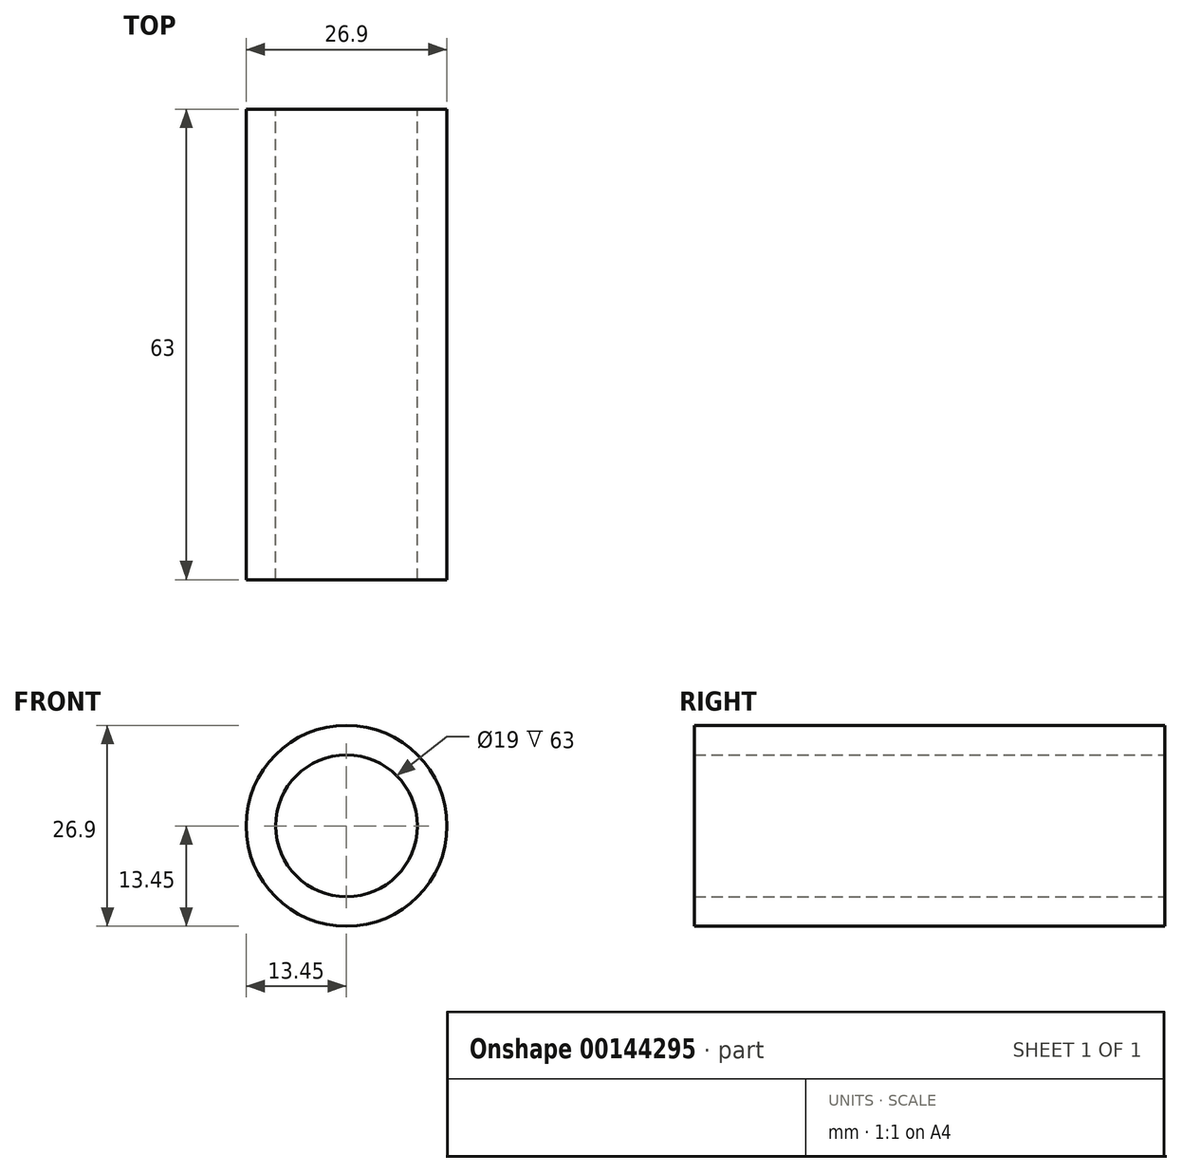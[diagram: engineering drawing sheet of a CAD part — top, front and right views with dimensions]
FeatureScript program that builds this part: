
annotation { "Feature Type Name" : "Feature", "Feature Type Description" : "" }
export const myFeature = defineFeature(function(context is Context, id is Id, definition is map)
    precondition{}
    {
        {
            var Q0;
            Q0=qCreatedBy(makeId("Front.planeOp"),FACE);
            var sketch = newSketch(context, id + "F0", { "sketchPlane" : qUnion([Q0])});
            skCircle(sketch, "E0", {"center": v(0, 0) * mm, "radius": 13.45 * mm});
            skCircle(sketch, "E1", {"center": v(0, 0) * mm, "radius": 9.5 * mm});
            skSolve(sketch);
        }
        {
            var Q0;
            Q0=makeQuery(id+"F0.imprint","IMPRINT",FACE,{"disambiguationData":[TD([[makeQuery(id+"F0.imprint","IMPRINT",EDGE,{"derivedFrom":sQuery(id+"F0.wireOp",EDGE,"E0")}),1.0]])]});
            extrude(context, id + "F1", {"entities" : qUnion([Q0]), "depth" : 63 * mm});
        }
    });
